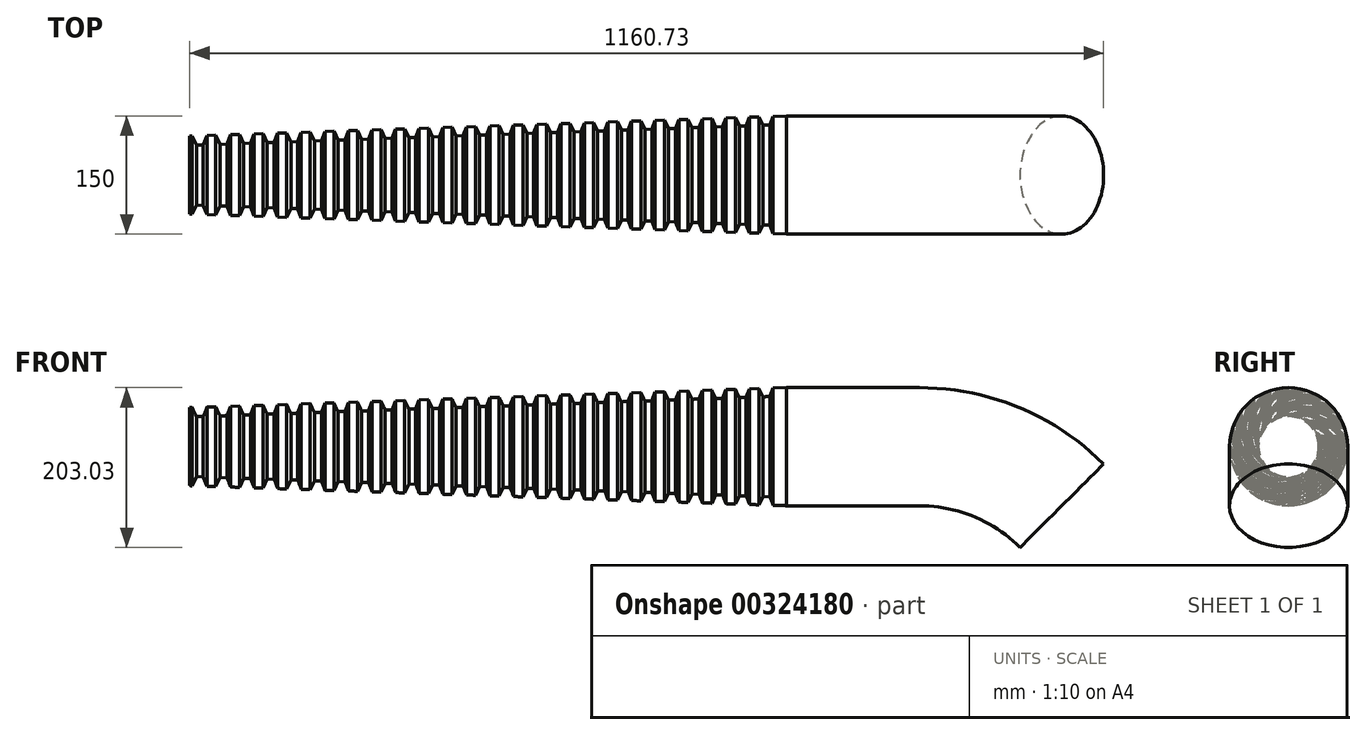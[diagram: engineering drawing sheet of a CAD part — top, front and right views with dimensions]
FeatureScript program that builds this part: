
annotation { "Feature Type Name" : "Feature", "Feature Type Description" : "" }
export const myFeature = defineFeature(function(context is Context, id is Id, definition is map)
    precondition{}
    {
        {
            var Q0;
            Q0=qCreatedBy(makeId("Front.planeOp"),FACE);
            var sketch = newSketch(context, id + "F0", { "sketchPlane" : qUnion([Q0])});
            skLineSegment(sketch, "E0", {"start": v(-350, 0) * mm, "end": v(-181.07, 0) * mm, "construction": true});
            skLineSegment(sketch, "E1", {"start": v(0, -181.07) * mm, "end": v(0, -350) * mm, "construction": true});
            skLineSegment(sketch, "E2", {"start": v(0, -350) * mm, "end": v(150, -350) * mm, "construction": true});
            skLineSegment(sketch, "E3", {"start": v(150, -350) * mm, "end": v(150, -181.07) * mm, "construction": true});
            skLineSegment(sketch, "E4", {"start": v(-181.07, 150) * mm, "end": v(-350, 150) * mm, "construction": true});
            skLineSegment(sketch, "E5", {"start": v(-350, 150) * mm, "end": v(-350, 0) * mm, "construction": true});
            skPoint(sketch, "E6.visualSharp", {"position": v(0, 0) * mm});
            skArc(sketch, "E6.filletArc", {"start": v(0, -181.07) * mm, "mid": v(-53.03, -53.03) * mm, "end": v(-181.07, 0) * mm, "construction": true});
            skPoint(sketch, "E7.visualSharp", {"position": v(150, 150) * mm});
            skArc(sketch, "E7.filletArc", {"start": v(150, -181.07) * mm, "mid": v(53.03, 53.03) * mm, "end": v(-181.07, 150) * mm, "construction": true});
            skLineSegment(sketch, "E8.0", {"start": v(-181.07, 75) * mm, "end": v(-350, 75) * mm});
            skArc(sketch, "E8.1", {"start": v(75, -181.07) * mm, "mid": v(0, 0) * mm, "end": v(-181.07, 75) * mm});
            skLineSegment(sketch, "E8.2", {"start": v(75, -350) * mm, "end": v(75, -181.07) * mm});
            skPoint(sketch, "E9.1.internal.snap0", {"position": v(-265.53, 0) * mm});
            skSolve(sketch);
        }
        {
            var Q0;
            Q0=sQuery(id+"F0.wireOp",EDGE,"E5");
            cPoint(context, id + "F1", {"entities" : qUnion([Q0]), "parameter" : 0.5});
        }
        {
            var Q0;
            Q0=qCreatedBy(makeId("Right.planeOp"),FACE);
            var Q1;
            Q1 = qCreatedBy(id + "F1" ,VERTEX);
            cPlane(context, id + "F2", {"entities" : qUnion([Q0, Q1]), "cplaneType" : CPlaneType.PLANE_POINT, "offset" : 25 * mm, "width" : 150 * mm, "height" : 150 * mm});
        }
        {
            var Q0;
            Q0=qCreatedBy(id+"F2.planeOp",FACE);
            var sketch = newSketch(context, id + "F3", { "sketchPlane" : qUnion([Q0])});
            skCircle(sketch, "E10", {"center": v(0, 75) * mm, "radius": 75 * mm});
            skSolve(sketch);
        }
        {
            var Q0;
            Q0=makeQuery(id+"F3.imprint","IMPRINT",FACE,{"disambiguationData":[TD([[makeQuery(id+"F3.imprint","IMPRINT",EDGE,{"derivedFrom":sQuery(id+"F3.wireOp",EDGE,"E10")}),1.0]])]});
            var Q1;
            Q1 = qConstructionFilter(qBodyType(qCreatedBy(id + "F0" ,EDGE), BodyType.WIRE), ConstructionObject.NO);
            sweep(context, id + "F4", {"profiles" : qUnion([Q0]), "path" : qUnion([Q1])});
        }
        {
            var Q0;
            Q0=qCreatedBy(makeId("Right.planeOp"),FACE);
            var sketch = newSketch(context, id + "F5", { "sketchPlane" : qUnion([Q0])});
            skLineSegment(sketch, "E11", {"start": v(-76.86, 0) * mm, "end": v(96.35, 0) * mm, "construction": true});
            skSolve(sketch);
        }
        {
            var Q0;
            Q0=qCreatedBy(makeId("Front.planeOp"),FACE);
            var sketch = newSketch(context, id + "F6", { "sketchPlane" : qUnion([Q0])});
            skLineSegment(sketch, "E12", {"start": v(-350, 0) * mm, "end": v(-1107.7, 25.46) * mm});
            skLineSegment(sketch, "E13", {"start": v(-1107.7, 124.54) * mm, "end": v(-350, 150) * mm});
            skLineSegment(sketch, "E14", {"start": v(-181.07, 150) * mm, "end": v(-350, 150) * mm, "construction": true});
            skLineSegment(sketch, "E15", {"start": v(-350, 0) * mm, "end": v(-181.07, 0) * mm, "construction": true});
            skLineSegment(sketch, "E16", {"start": v(-350, 75) * mm, "end": v(-868.1, 75) * mm, "construction": true});
            skSolve(sketch);
        }
        {
            var Q0;
            Q0=sQuery(id+"F6.wireOp",VERTEX,"E13.start");
            var Q1;
            Q1=qCreatedBy(id+"F2.planeOp",FACE);
            cPlane(context, id + "F7", {"entities" : qUnion([Q0, Q1]), "cplaneType" : CPlaneType.PLANE_POINT, "offset" : 25 * mm, "width" : 150 * mm, "height" : 150 * mm});
        }
        {
            var Q0;
            Q0=qCreatedBy(id+"F7.planeOp",FACE);
            var sketch = newSketch(context, id + "F8", { "sketchPlane" : qUnion([Q0])});
            skCircle(sketch, "E17", {"center": v(0, 75) * mm, "radius": 49.54 * mm});
            skSolve(sketch);
        }
        {
            var Q1;
            Q1=makeQuery(id+"F8.imprint","IMPRINT",FACE,{"disambiguationData":[TD([[makeQuery(id+"F8.imprint","IMPRINT",EDGE,{"derivedFrom":sQuery(id+"F8.wireOp",EDGE,"E17")}),1.0]])]});
            var Q2;
            Q2=makeQuery(id+"F3.imprint","IMPRINT",FACE,{"disambiguationData":[TD([[makeQuery(id+"F3.imprint","IMPRINT",EDGE,{"derivedFrom":sQuery(id+"F3.wireOp",EDGE,"E10")}),1.0]])]});
            var Q3;
            Q3=sQuery(id+"F6.wireOp",EDGE,"E13");
            var Q4;
            Q4=sQuery(id+"F6.wireOp",EDGE,"E12");
            loft(context, id + "F9", {"operationType" : NewBodyOperationType.ADD, "addGuides" : true, "sheetProfilesArray" : [{ "sheetProfileEntities" : qUnion([Q1]) }, { "sheetProfileEntities" : qUnion([Q2]) }], "guidesArray" : [{ "guideEntities" : qUnion([Q3]), "guideDerivativeType" : LoftGuideDerivativeType.DEFAULT, "guideDerivativeMagnitude" : 1 }, { "guideEntities" : qUnion([Q4]), "guideDerivativeType" : LoftGuideDerivativeType.DEFAULT, "guideDerivativeMagnitude" : 1 }]});
        }
        {
            var Q0;
            Q0=qCreatedBy(makeId("Front.planeOp"),FACE);
            var sketch = newSketch(context, id + "F10", { "sketchPlane" : qUnion([Q0])});
            skLineSegment(sketch, "E18", {"start": v(-1104.7, 124.64) * mm, "end": v(-1099.27, 113.07) * mm});
            skLineSegment(sketch, "E19", {"start": v(-1099.27, 113.07) * mm, "end": v(-1090.51, 113.37) * mm});
            skLineSegment(sketch, "E20", {"start": v(-1090.51, 113.37) * mm, "end": v(-1085.87, 125.27) * mm});
            skLineSegment(sketch, "E21", {"start": v(-1085.87, 125.27) * mm, "end": v(-1104.7, 124.64) * mm});
            skLineSegment(sketch, "E22.1.0.0", {"start": v(-1055.89, 126.32) * mm, "end": v(-1074.72, 125.7) * mm});
            skLineSegment(sketch, "E22.1.0.1", {"start": v(-1069.28, 114.13) * mm, "end": v(-1060.53, 114.42) * mm});
            skLineSegment(sketch, "E22.1.0.2", {"start": v(-1074.72, 125.7) * mm, "end": v(-1069.28, 114.13) * mm});
            skLineSegment(sketch, "E22.1.0.3", {"start": v(-1060.53, 114.42) * mm, "end": v(-1055.89, 126.32) * mm});
            skLineSegment(sketch, "E22.2.0.0", {"start": v(-1025.9, 127.38) * mm, "end": v(-1044.73, 126.75) * mm});
            skLineSegment(sketch, "E22.2.0.1", {"start": v(-1039.3, 115.18) * mm, "end": v(-1030.55, 115.47) * mm});
            skLineSegment(sketch, "E22.2.0.2", {"start": v(-1044.73, 126.75) * mm, "end": v(-1039.3, 115.18) * mm});
            skLineSegment(sketch, "E22.2.0.3", {"start": v(-1030.55, 115.47) * mm, "end": v(-1025.9, 127.38) * mm});
            skLineSegment(sketch, "E22.3.0.0", {"start": v(-995.92, 128.43) * mm, "end": v(-1014.75, 127.8) * mm});
            skLineSegment(sketch, "E22.3.0.1", {"start": v(-1009.32, 116.23) * mm, "end": v(-1000.57, 116.53) * mm});
            skLineSegment(sketch, "E22.3.0.2", {"start": v(-1014.75, 127.8) * mm, "end": v(-1009.32, 116.23) * mm});
            skLineSegment(sketch, "E22.3.0.3", {"start": v(-1000.57, 116.53) * mm, "end": v(-995.92, 128.43) * mm});
            skLineSegment(sketch, "E22.4.0.0", {"start": v(-965.94, 129.49) * mm, "end": v(-984.77, 128.85) * mm});
            skLineSegment(sketch, "E22.4.0.1", {"start": v(-979.34, 117.29) * mm, "end": v(-970.59, 117.58) * mm});
            skLineSegment(sketch, "E22.4.0.2", {"start": v(-984.77, 128.85) * mm, "end": v(-979.34, 117.29) * mm});
            skLineSegment(sketch, "E22.4.0.3", {"start": v(-970.59, 117.58) * mm, "end": v(-965.94, 129.49) * mm});
            skLineSegment(sketch, "E22.5.0.0", {"start": v(-935.96, 130.54) * mm, "end": v(-954.8, 129.9) * mm});
            skLineSegment(sketch, "E22.5.0.1", {"start": v(-949.36, 118.34) * mm, "end": v(-940.6, 118.63) * mm});
            skLineSegment(sketch, "E22.5.0.2", {"start": v(-954.8, 129.9) * mm, "end": v(-949.36, 118.34) * mm});
            skLineSegment(sketch, "E22.5.0.3", {"start": v(-940.6, 118.63) * mm, "end": v(-935.96, 130.54) * mm});
            skLineSegment(sketch, "E22.6.0.0", {"start": v(-905.98, 131.6) * mm, "end": v(-924.8, 130.96) * mm});
            skLineSegment(sketch, "E22.6.0.1", {"start": v(-919.38, 119.4) * mm, "end": v(-910.62, 119.69) * mm});
            skLineSegment(sketch, "E22.6.0.2", {"start": v(-924.8, 130.96) * mm, "end": v(-919.38, 119.4) * mm});
            skLineSegment(sketch, "E22.6.0.3", {"start": v(-910.62, 119.69) * mm, "end": v(-905.98, 131.6) * mm});
            skLineSegment(sketch, "E22.7.0.0", {"start": v(-876, 132.65) * mm, "end": v(-894.83, 132.01) * mm});
            skLineSegment(sketch, "E22.7.0.1", {"start": v(-889.4, 120.45) * mm, "end": v(-880.64, 120.74) * mm});
            skLineSegment(sketch, "E22.7.0.2", {"start": v(-894.83, 132.01) * mm, "end": v(-889.4, 120.45) * mm});
            skLineSegment(sketch, "E22.7.0.3", {"start": v(-880.64, 120.74) * mm, "end": v(-876, 132.65) * mm});
            skLineSegment(sketch, "E22.8.0.0", {"start": v(-846.02, 133.7) * mm, "end": v(-864.85, 133.07) * mm});
            skLineSegment(sketch, "E22.8.0.1", {"start": v(-859.41, 121.5) * mm, "end": v(-850.66, 121.8) * mm});
            skLineSegment(sketch, "E22.8.0.2", {"start": v(-864.85, 133.07) * mm, "end": v(-859.41, 121.5) * mm});
            skLineSegment(sketch, "E22.8.0.3", {"start": v(-850.66, 121.8) * mm, "end": v(-846.02, 133.7) * mm});
            skLineSegment(sketch, "E22.9.0.0", {"start": v(-816.04, 134.75) * mm, "end": v(-834.86, 134.12) * mm});
            skLineSegment(sketch, "E22.9.0.1", {"start": v(-829.43, 122.56) * mm, "end": v(-820.68, 122.85) * mm});
            skLineSegment(sketch, "E22.9.0.2", {"start": v(-834.86, 134.12) * mm, "end": v(-829.43, 122.56) * mm});
            skLineSegment(sketch, "E22.9.0.3", {"start": v(-820.68, 122.85) * mm, "end": v(-816.04, 134.75) * mm});
            skLineSegment(sketch, "E22.10.0.0", {"start": v(-786.05, 135.8) * mm, "end": v(-804.88, 135.17) * mm});
            skLineSegment(sketch, "E22.10.0.1", {"start": v(-799.45, 123.6) * mm, "end": v(-790.7, 123.9) * mm});
            skLineSegment(sketch, "E22.10.0.2", {"start": v(-804.88, 135.17) * mm, "end": v(-799.45, 123.6) * mm});
            skLineSegment(sketch, "E22.10.0.3", {"start": v(-790.7, 123.9) * mm, "end": v(-786.05, 135.8) * mm});
            skLineSegment(sketch, "E22.11.0.0", {"start": v(-756.07, 136.86) * mm, "end": v(-774.9, 136.23) * mm});
            skLineSegment(sketch, "E22.11.0.1", {"start": v(-769.47, 124.66) * mm, "end": v(-760.72, 124.96) * mm});
            skLineSegment(sketch, "E22.11.0.2", {"start": v(-774.9, 136.23) * mm, "end": v(-769.47, 124.66) * mm});
            skLineSegment(sketch, "E22.11.0.3", {"start": v(-760.72, 124.96) * mm, "end": v(-756.07, 136.86) * mm});
            skLineSegment(sketch, "E22.direction1", {"start": v(-1099.27, 113.07) * mm, "end": v(-1069.28, 114.13) * mm, "construction": true});
            skLineSegment(sketch, "E23.0.12.0", {"start": v(-726.1, 137.91) * mm, "end": v(-744.92, 137.28) * mm});
            skLineSegment(sketch, "E23.3.12.0", {"start": v(-739.49, 125.72) * mm, "end": v(-730.73, 126.01) * mm});
            skLineSegment(sketch, "E23.6.12.0", {"start": v(-744.92, 137.28) * mm, "end": v(-739.49, 125.72) * mm});
            skLineSegment(sketch, "E23.9.12.0", {"start": v(-730.73, 126.01) * mm, "end": v(-726.1, 137.91) * mm});
            skLineSegment(sketch, "E23.0.13.0", {"start": v(-696.1, 138.97) * mm, "end": v(-714.94, 138.34) * mm});
            skLineSegment(sketch, "E23.3.13.0", {"start": v(-709.5, 126.77) * mm, "end": v(-700.75, 127.06) * mm});
            skLineSegment(sketch, "E23.6.13.0", {"start": v(-714.94, 138.34) * mm, "end": v(-709.5, 126.77) * mm});
            skLineSegment(sketch, "E23.9.13.0", {"start": v(-700.75, 127.06) * mm, "end": v(-696.1, 138.97) * mm});
            skLineSegment(sketch, "E23.0.14.0", {"start": v(-666.13, 140.02) * mm, "end": v(-684.96, 139.39) * mm});
            skLineSegment(sketch, "E23.3.14.0", {"start": v(-679.53, 127.82) * mm, "end": v(-670.77, 128.12) * mm});
            skLineSegment(sketch, "E23.6.14.0", {"start": v(-684.96, 139.39) * mm, "end": v(-679.53, 127.82) * mm});
            skLineSegment(sketch, "E23.9.14.0", {"start": v(-670.77, 128.12) * mm, "end": v(-666.13, 140.02) * mm});
            skLineSegment(sketch, "E23.0.15.0", {"start": v(-636.15, 141.08) * mm, "end": v(-654.98, 140.44) * mm});
            skLineSegment(sketch, "E23.3.15.0", {"start": v(-649.54, 128.88) * mm, "end": v(-640.79, 129.17) * mm});
            skLineSegment(sketch, "E23.6.15.0", {"start": v(-654.98, 140.44) * mm, "end": v(-649.54, 128.88) * mm});
            skLineSegment(sketch, "E23.9.15.0", {"start": v(-640.79, 129.17) * mm, "end": v(-636.15, 141.08) * mm});
            skLineSegment(sketch, "E23.0.16.0", {"start": v(-606.17, 142.13) * mm, "end": v(-625, 141.5) * mm});
            skLineSegment(sketch, "E23.3.16.0", {"start": v(-619.56, 129.93) * mm, "end": v(-610.8, 130.22) * mm});
            skLineSegment(sketch, "E23.6.16.0", {"start": v(-625, 141.5) * mm, "end": v(-619.56, 129.93) * mm});
            skLineSegment(sketch, "E23.9.16.0", {"start": v(-610.8, 130.22) * mm, "end": v(-606.17, 142.13) * mm});
            skLineSegment(sketch, "E23.0.17.0", {"start": v(-576.18, 143.18) * mm, "end": v(-595.01, 142.55) * mm});
            skLineSegment(sketch, "E23.3.17.0", {"start": v(-589.58, 130.98) * mm, "end": v(-580.83, 131.28) * mm});
            skLineSegment(sketch, "E23.6.17.0", {"start": v(-595.01, 142.55) * mm, "end": v(-589.58, 130.98) * mm});
            skLineSegment(sketch, "E23.9.17.0", {"start": v(-580.83, 131.28) * mm, "end": v(-576.18, 143.18) * mm});
            skLineSegment(sketch, "E23.0.18.0", {"start": v(-546.2, 144.24) * mm, "end": v(-565.03, 143.6) * mm});
            skLineSegment(sketch, "E23.3.18.0", {"start": v(-559.6, 132.04) * mm, "end": v(-550.84, 132.33) * mm});
            skLineSegment(sketch, "E23.6.18.0", {"start": v(-565.03, 143.6) * mm, "end": v(-559.6, 132.04) * mm});
            skLineSegment(sketch, "E23.9.18.0", {"start": v(-550.84, 132.33) * mm, "end": v(-546.2, 144.24) * mm});
            skLineSegment(sketch, "E23.0.19.0", {"start": v(-516.22, 145.29) * mm, "end": v(-535.05, 144.66) * mm});
            skLineSegment(sketch, "E23.3.19.0", {"start": v(-529.62, 133.1) * mm, "end": v(-520.86, 133.39) * mm});
            skLineSegment(sketch, "E23.6.19.0", {"start": v(-535.05, 144.66) * mm, "end": v(-529.62, 133.1) * mm});
            skLineSegment(sketch, "E23.9.19.0", {"start": v(-520.86, 133.39) * mm, "end": v(-516.22, 145.29) * mm});
            skLineSegment(sketch, "E23.0.20.0", {"start": v(-486.24, 146.34) * mm, "end": v(-505.07, 145.71) * mm});
            skLineSegment(sketch, "E23.3.20.0", {"start": v(-499.64, 134.14) * mm, "end": v(-490.88, 134.44) * mm});
            skLineSegment(sketch, "E23.6.20.0", {"start": v(-505.07, 145.71) * mm, "end": v(-499.64, 134.14) * mm});
            skLineSegment(sketch, "E23.9.20.0", {"start": v(-490.88, 134.44) * mm, "end": v(-486.24, 146.34) * mm});
            skLineSegment(sketch, "E23.0.21.0", {"start": v(-456.26, 147.4) * mm, "end": v(-475.09, 146.76) * mm});
            skLineSegment(sketch, "E23.3.21.0", {"start": v(-469.66, 135.2) * mm, "end": v(-460.9, 135.5) * mm});
            skLineSegment(sketch, "E23.6.21.0", {"start": v(-475.09, 146.76) * mm, "end": v(-469.66, 135.2) * mm});
            skLineSegment(sketch, "E23.9.21.0", {"start": v(-460.9, 135.5) * mm, "end": v(-456.26, 147.4) * mm});
            skLineSegment(sketch, "E23.0.22.0", {"start": v(-426.28, 148.45) * mm, "end": v(-445.1, 147.82) * mm});
            skLineSegment(sketch, "E23.3.22.0", {"start": v(-439.67, 136.25) * mm, "end": v(-430.92, 136.55) * mm});
            skLineSegment(sketch, "E23.6.22.0", {"start": v(-445.1, 147.82) * mm, "end": v(-439.67, 136.25) * mm});
            skLineSegment(sketch, "E23.9.22.0", {"start": v(-430.92, 136.55) * mm, "end": v(-426.28, 148.45) * mm});
            skLineSegment(sketch, "E23.0.23.0", {"start": v(-396.3, 149.5) * mm, "end": v(-415.12, 148.87) * mm});
            skLineSegment(sketch, "E23.3.23.0", {"start": v(-409.7, 137.3) * mm, "end": v(-400.94, 137.6) * mm});
            skLineSegment(sketch, "E23.6.23.0", {"start": v(-415.12, 148.87) * mm, "end": v(-409.7, 137.3) * mm});
            skLineSegment(sketch, "E23.9.23.0", {"start": v(-400.94, 137.6) * mm, "end": v(-396.3, 149.5) * mm});
            skLineSegment(sketch, "E23.0.24.0", {"start": v(-366.31, 150.56) * mm, "end": v(-385.14, 149.93) * mm});
            skLineSegment(sketch, "E23.3.24.0", {"start": v(-379.71, 138.36) * mm, "end": v(-370.96, 138.65) * mm});
            skLineSegment(sketch, "E23.6.24.0", {"start": v(-385.14, 149.93) * mm, "end": v(-379.71, 138.36) * mm});
            skLineSegment(sketch, "E23.9.24.0", {"start": v(-370.96, 138.65) * mm, "end": v(-366.31, 150.56) * mm});
            skSolve(sketch);
        }
        {
            var Q0;
            Q0 = qSketchRegion(id + "F10", true);
            var Q1;
            Q1=sQuery(id+"F6.wireOp",EDGE,"E16");
            revolve(context, id + "F11", {"operationType" : NewBodyOperationType.REMOVE, "entities" : qUnion([Q0]), "axis" : qUnion([Q1]), "revolveType" : RevolveType.FULL, "oppositeDirection" : true});
        }
        {
            var Q0;
            Q0=qCreatedBy(makeId("Front.planeOp"),FACE);
            var sketch = newSketch(context, id + "F12", { "sketchPlane" : qUnion([Q0])});
            skLineSegment(sketch, "E24", {"start": v(-114.67, -114.67) * mm, "end": v(98.13, 98.13) * mm});
            skLineSegment(sketch, "E25", {"start": v(98.13, 98.13) * mm, "end": v(441.93, -378.46) * mm});
            skLineSegment(sketch, "E26", {"start": v(441.93, -378.46) * mm, "end": v(-121.55, -389.8) * mm});
            skLineSegment(sketch, "E27", {"start": v(-121.55, -389.8) * mm, "end": v(-114.67, -114.67) * mm});
            skSolve(sketch);
        }
        {
            var Q0;
            Q0=makeQuery(id+"F12.imprint","IMPRINT",FACE,{"disambiguationData":[TD([[makeQuery(id+"F12.imprint","IMPRINT",EDGE,{"derivedFrom":sQuery(id+"F12.wireOp",EDGE,"E24")}),-1.0]])]});
            extrude(context, id + "F13", {"entities" : qUnion([Q0]), "operationType" : NewBodyOperationType.REMOVE, "endBound" : BoundingType.SYMMETRIC, "depth" : 464 * mm});
        }
    });
